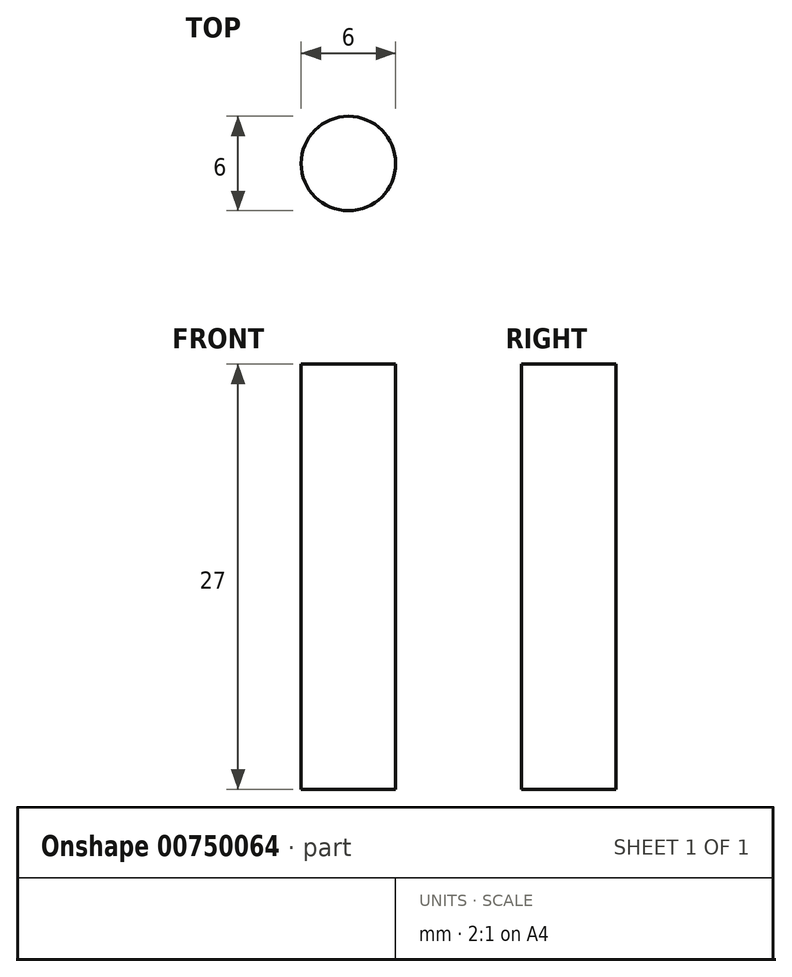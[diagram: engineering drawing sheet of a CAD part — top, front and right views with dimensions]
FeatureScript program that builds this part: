
annotation { "Feature Type Name" : "Feature", "Feature Type Description" : "" }
export const myFeature = defineFeature(function(context is Context, id is Id, definition is map)
    precondition{}
    {
        {
            var Q0;
            Q0=qCreatedBy(makeId("Top.planeOp"),FACE);
            var sketch = newSketch(context, id + "F0", { "sketchPlane" : qUnion([Q0])});
            skCircle(sketch, "E0", {"center": v(0, 0) * mm, "radius": 3 * mm});
            skSolve(sketch);
        }
        {
            var Q0;
            Q0=makeQuery(id+"F0.imprint","IMPRINT",FACE,{"disambiguationData":[TD([[makeQuery(id+"F0.imprint","IMPRINT",EDGE,{"derivedFrom":sQuery(id+"F0.wireOp",EDGE,"E0")}),1.0]])]});
            extrude(context, id + "F1", {"entities" : qUnion([Q0]), "depth" : 27 * mm, "offsetDistance" : 25 * mm});
        }
    });
